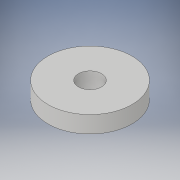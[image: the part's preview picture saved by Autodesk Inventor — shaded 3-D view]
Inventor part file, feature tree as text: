
AUTODESK INVENTOR PART (.ipt)
format: ipt  version: 2018 (Build 220112000, 112)  size: 98,816 bytes
history: native  units: in
note: dims shown in document units (in); Inventor stores cm internally (conversion verified against a paired STEP export)
features: sketch x2, extrude x1, hole x1
ambient origin geometry x8: Origin, YZ Plane, XZ Plane, XY Plane, X Axis, Y Axis, Z Axis, Center Point
bodies: Solid1 (feature_tree)
feature tree (4):
  extrude  "Extrusion1"  Depth=0.08in TaperAngle=0.0deg
  hole  "Hole1"  [1 undecoded]
  sketch  "Sketch1"  dims[d0=0.4in d1=0.08in d2=0.0in]
  sketch  "Sketch2"  dims[d3=0.11in d4=0.11in d5=0.75in d6=0.375in d7=0.25in d8=0.5635in d9=1.0in d10=0.8108in]
note: 1 required parameter value undecoded (feature->parameter linkage not recoverable at this tier; creation-order binding heuristic only, values carry confidence <= 0.55)
